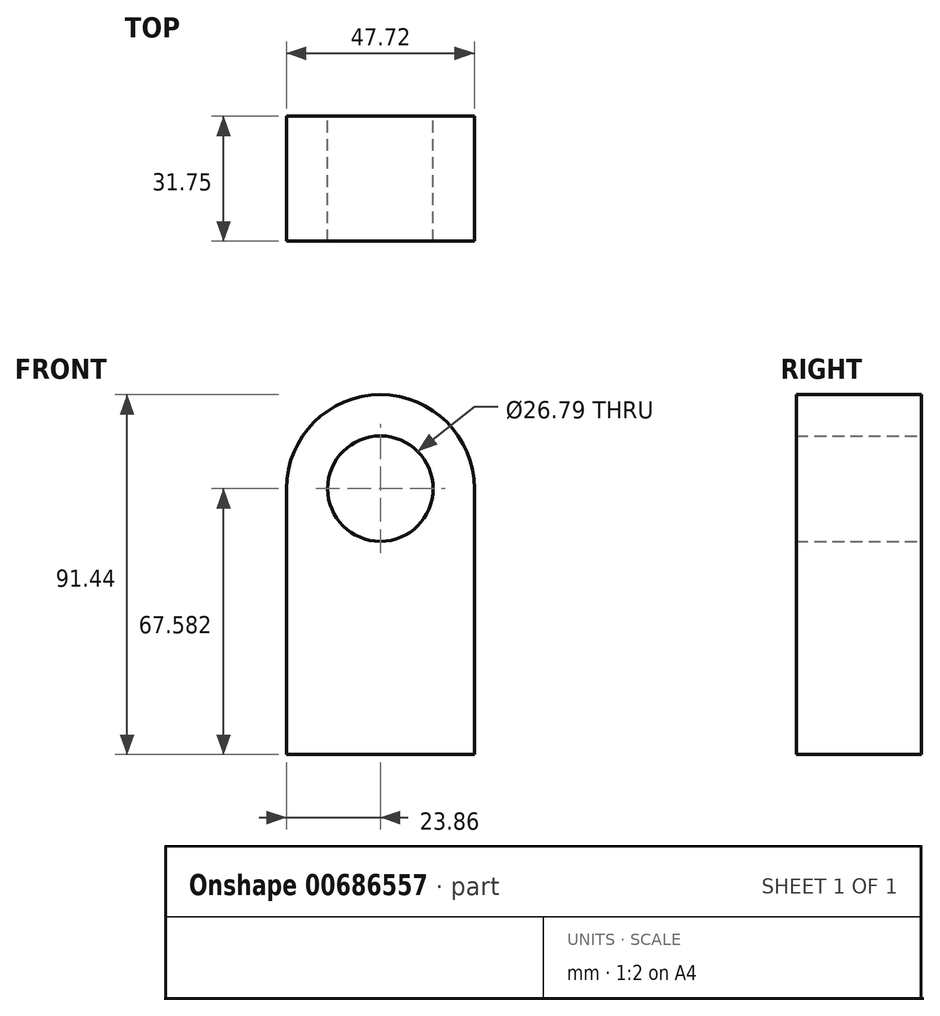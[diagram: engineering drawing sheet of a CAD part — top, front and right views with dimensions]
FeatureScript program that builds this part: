
annotation { "Feature Type Name" : "Feature", "Feature Type Description" : "" }
export const myFeature = defineFeature(function(context is Context, id is Id, definition is map)
    precondition{}
    {
        {
            var Q0;
            Q0=qCreatedBy(makeId("Front.planeOp"),FACE);
            var sketch = newSketch(context, id + "F0", { "sketchPlane" : qUnion([Q0])});
            skLineSegment(sketch, "E0.top", {"start": v(23.86, -33.8) * mm, "end": v(-23.86, -33.8) * mm});
            skLineSegment(sketch, "E0.left", {"start": v(23.86, 33.8) * mm, "end": v(23.86, -33.8) * mm});
            skLineSegment(sketch, "E0.right", {"start": v(-23.86, 33.8) * mm, "end": v(-23.86, -33.8) * mm});
            skPoint(sketch, "E0.middle", {"position": v(0, 0) * mm});
            skArc(sketch, "E1", {"start": v(23.86, 33.8) * mm, "mid": v(0, 57.65) * mm, "end": v(-23.86, 33.8) * mm});
            skCircle(sketch, "E2", {"center": v(0, 33.8) * mm, "radius": 13.4 * mm});
            skSolve(sketch);
        }
        {
            var Q0;
            Q0=makeQuery(id+"F0.imprint","IMPRINT",FACE,{"disambiguationData":[TD([[makeQuery(id+"F0.imprint","IMPRINT",EDGE,{"derivedFrom":sQuery(id+"F0.wireOp",EDGE,"E0.top")}),-1.0]])]});
            extrude(context, id + "F1", {"entities" : qUnion([Q0]), "depth" : 31.75 * mm, "offsetDistance" : 25.4 * mm});
        }
    });
